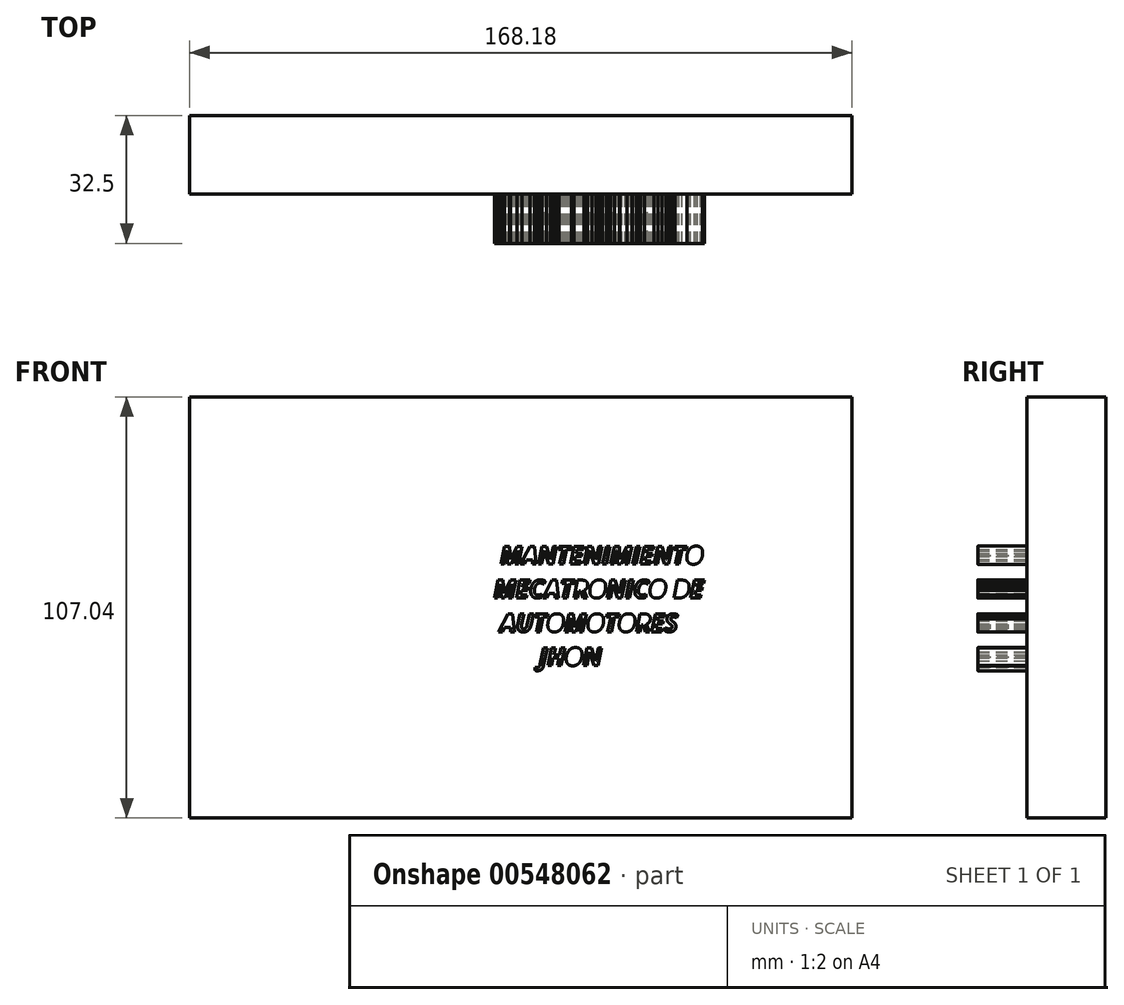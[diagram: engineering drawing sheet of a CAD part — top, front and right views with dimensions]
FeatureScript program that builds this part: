
annotation { "Feature Type Name" : "Feature", "Feature Type Description" : "" }
export const myFeature = defineFeature(function(context is Context, id is Id, definition is map)
    precondition{}
    {
        {
            var Q0;
            Q0=qCreatedBy(makeId("Front.planeOp"),FACE);
            var sketch = newSketch(context, id + "F0", { "sketchPlane" : qUnion([Q0])});
            skLineSegment(sketch, "E0.bottom", {"start": v(71.6, 53.52) * mm, "end": v(-71.6, 53.52) * mm});
            skLineSegment(sketch, "E0.top", {"start": v(71.6, -53.52) * mm, "end": v(-71.6, -53.52) * mm});
            skLineSegment(sketch, "E0.left", {"start": v(71.6, 53.52) * mm, "end": v(71.6, -53.52) * mm});
            skLineSegment(sketch, "E0.right", {"start": v(-71.6, 53.52) * mm, "end": v(-71.6, -53.52) * mm});
            skPoint(sketch, "E0.middle", {"position": v(0, 0) * mm});
            skSolve(sketch);
        }
        {
            var Q0;
            Q0=makeQuery(id+"F0.imprint","IMPRINT",FACE,{"disambiguationData":[TD([[makeQuery(id+"F0.imprint","IMPRINT",EDGE,{"derivedFrom":sQuery(id+"F0.wireOp",EDGE,"E0.bottom")}),1.0]])]});
            extrude(context, id + "F1", {"entities" : qUnion([Q0]), "depth" : 20 * mm, "offsetDistance" : 25 * mm});
        }
        {
            var Q0;
            Q0=makeQuery(id+"F1.opExtrude","CAP_FACE",FACE,{"disambiguationData":[OSD([sQuery(id+"F0.wireOp",EDGE,"E0.bottom"),sQuery(id+"F0.wireOp",EDGE,"E0.top"),sQuery(id+"F0.wireOp",EDGE,"E0.left"),sQuery(id+"F0.wireOp",EDGE,"E0.right")])],"isStart":false});
            var sketch = newSketch(context, id + "F2", { "sketchPlane" : qUnion([Q0])});
            skText(sketch, "E1", { "text": "         MANTENIMIENTO  \n        MECATRONICO DE \n         AUTOMOTORES \n               JHON ", "fontName": "OpenSans-BoldItalic.ttf"});
            const initialGuessF2  = {"E1": [-0.0325, 0.01102, 1, 0, 0.00455]};
            skSetInitialGuess(sketch, initialGuessF2);
            skSolve(sketch);
        }
        {
            var Q0;
            Q0=makeQuery(id+"F1.opExtrude","SWEPT_FACE",FACE,{"disambiguationData":[OSD([sQuery(id+"F0.wireOp",EDGE,"E0.right")])]});
            extrude(context, id + "F3", {"entities" : qUnion([Q0]), "operationType" : NewBodyOperationType.ADD, "depth" : 25 * mm, "offsetDistance" : 25 * mm});
        }
        {
            var Q0;
            Q0 = qSketchRegion(id + "F2", true);
            var Q1;
            Q1=makeQuery(id+"F2.imprint","IMPRINT",FACE,{"disambiguationData":[TD([[makeQuery(id+"F2.imprint","IMPRINT",EDGE,{"derivedFrom":sQuery(id+"F2.wireOp",EDGE,"E1.sketch_text.stroke-262")}),1.0]])]});
            var Q2;
            Q2=makeQuery(id+"F2.imprint","IMPRINT",FACE,{"disambiguationData":[TD([[makeQuery(id+"F2.imprint","IMPRINT",EDGE,{"derivedFrom":sQuery(id+"F2.wireOp",EDGE,"E1.sketch_text.stroke-181")}),-1.0]])]});
            var Q3;
            Q3=makeQuery(id+"F2.imprint","IMPRINT",FACE,{"disambiguationData":[TD([[makeQuery(id+"F2.imprint","IMPRINT",EDGE,{"derivedFrom":sQuery(id+"F2.wireOp",EDGE,"E1.sketch_text.stroke-32")}),-1.0]])]});
            var Q4;
            Q4=makeQuery(id+"F2.imprint","IMPRINT",FACE,{"disambiguationData":[TD([[makeQuery(id+"F2.imprint","IMPRINT",EDGE,{"derivedFrom":sQuery(id+"F2.wireOp",EDGE,"E1.sketch_text.stroke-511")}),-1.0]])]});
            var Q5;
            Q5=makeQuery(id+"F2.imprint","IMPRINT",FACE,{"disambiguationData":[TD([[makeQuery(id+"F2.imprint","IMPRINT",EDGE,{"derivedFrom":sQuery(id+"F2.wireOp",EDGE,"E1.sketch_text.stroke-67")}),-1.0]])]});
            var Q6;
            Q6=makeQuery(id+"F2.imprint","IMPRINT",FACE,{"disambiguationData":[TD([[makeQuery(id+"F2.imprint","IMPRINT",EDGE,{"derivedFrom":sQuery(id+"F2.wireOp",EDGE,"E1.sketch_text.stroke-104")}),-1.0]])]});
            var Q7;
            Q7=makeQuery(id+"F2.imprint","IMPRINT",FACE,{"disambiguationData":[TD([[makeQuery(id+"F2.imprint","IMPRINT",EDGE,{"derivedFrom":sQuery(id+"F2.wireOp",EDGE,"E1.sketch_text.stroke-153")}),1.0]])]});
            var Q8;
            Q8=makeQuery(id+"F2.imprint","IMPRINT",FACE,{"disambiguationData":[TD([[makeQuery(id+"F2.imprint","IMPRINT",EDGE,{"derivedFrom":sQuery(id+"F2.wireOp",EDGE,"E1.sketch_text.stroke-470")}),1.0]])]});
            var Q9;
            Q9=makeQuery(id+"F2.imprint","IMPRINT",FACE,{"disambiguationData":[TD([[makeQuery(id+"F2.imprint","IMPRINT",EDGE,{"derivedFrom":sQuery(id+"F2.wireOp",EDGE,"E1.sketch_text.stroke-452")}),-1.0]])]});
            var Q10;
            Q10=makeQuery(id+"F2.imprint","IMPRINT",FACE,{"disambiguationData":[TD([[makeQuery(id+"F2.imprint","IMPRINT",EDGE,{"derivedFrom":sQuery(id+"F2.wireOp",EDGE,"E1.sketch_text.stroke-442")}),1.0]])]});
            var Q11;
            Q11=makeQuery(id+"F2.imprint","IMPRINT",FACE,{"disambiguationData":[TD([[makeQuery(id+"F2.imprint","IMPRINT",EDGE,{"derivedFrom":sQuery(id+"F2.wireOp",EDGE,"E1.sketch_text.stroke-337")}),1.0]])]});
            var Q12;
            Q12=makeQuery(id+"F2.imprint","IMPRINT",FACE,{"disambiguationData":[TD([[makeQuery(id+"F2.imprint","IMPRINT",EDGE,{"derivedFrom":sQuery(id+"F2.wireOp",EDGE,"E1.sketch_text.stroke-319")}),1.0]])]});
            var Q13;
            Q13=makeQuery(id+"F2.imprint","IMPRINT",FACE,{"disambiguationData":[TD([[makeQuery(id+"F2.imprint","IMPRINT",EDGE,{"derivedFrom":sQuery(id+"F2.wireOp",EDGE,"E1.sketch_text.stroke-567")}),1.0]])]});
            var Q14;
            Q14=makeQuery(id+"F2.imprint","IMPRINT",FACE,{"disambiguationData":[TD([[makeQuery(id+"F2.imprint","IMPRINT",EDGE,{"derivedFrom":sQuery(id+"F2.wireOp",EDGE,"E1.sketch_text.stroke-432")}),-1.0]])]});
            var Q15;
            Q15=makeQuery(id+"F2.imprint","IMPRINT",FACE,{"disambiguationData":[TD([[makeQuery(id+"F2.imprint","IMPRINT",EDGE,{"derivedFrom":sQuery(id+"F2.wireOp",EDGE,"E1.sketch_text.stroke-480")}),1.0]])]});
            var Q16;
            Q16=makeQuery(id+"F2.imprint","IMPRINT",FACE,{"disambiguationData":[TD([[makeQuery(id+"F2.imprint","IMPRINT",EDGE,{"derivedFrom":sQuery(id+"F2.wireOp",EDGE,"E1.sketch_text.stroke-460")}),-1.0]])]});
            var Q17;
            Q17=makeQuery(id+"F2.imprint","IMPRINT",FACE,{"disambiguationData":[TD([[makeQuery(id+"F2.imprint","IMPRINT",EDGE,{"derivedFrom":sQuery(id+"F2.wireOp",EDGE,"E1.sketch_text.stroke-499")}),-1.0]])]});
            var Q18;
            Q18=makeQuery(id+"F2.imprint","IMPRINT",FACE,{"disambiguationData":[TD([[makeQuery(id+"F2.imprint","IMPRINT",EDGE,{"derivedFrom":sQuery(id+"F2.wireOp",EDGE,"E1.sketch_text.stroke-193")}),-1.0]])]});
            var Q19;
            Q19=makeQuery(id+"F2.imprint","IMPRINT",FACE,{"disambiguationData":[TD([[makeQuery(id+"F2.imprint","IMPRINT",EDGE,{"derivedFrom":sQuery(id+"F2.wireOp",EDGE,"E1.sketch_text.stroke-163")}),-1.0]])]});
            var Q20;
            Q20=makeQuery(id+"F2.imprint","IMPRINT",FACE,{"disambiguationData":[TD([[makeQuery(id+"F2.imprint","IMPRINT",EDGE,{"derivedFrom":sQuery(id+"F2.wireOp",EDGE,"E1.sketch_text.stroke-0")}),-1.0]])]});
            var Q21;
            Q21=makeQuery(id+"F2.imprint","IMPRINT",FACE,{"disambiguationData":[TD([[makeQuery(id+"F2.imprint","IMPRINT",EDGE,{"derivedFrom":sQuery(id+"F2.wireOp",EDGE,"E1.sketch_text.stroke-47")}),-1.0]])]});
            var Q22;
            Q22=makeQuery(id+"F2.imprint","IMPRINT",FACE,{"disambiguationData":[TD([[makeQuery(id+"F2.imprint","IMPRINT",EDGE,{"derivedFrom":sQuery(id+"F2.wireOp",EDGE,"E1.sketch_text.stroke-55")}),-1.0]])]});
            var Q23;
            Q23=makeQuery(id+"F2.imprint","IMPRINT",FACE,{"disambiguationData":[TD([[makeQuery(id+"F2.imprint","IMPRINT",EDGE,{"derivedFrom":sQuery(id+"F2.wireOp",EDGE,"E1.sketch_text.stroke-480")}),-1.0]])]});
            var Q24;
            Q24=makeQuery(id+"F2.imprint","IMPRINT",FACE,{"disambiguationData":[TD([[makeQuery(id+"F2.imprint","IMPRINT",EDGE,{"derivedFrom":sQuery(id+"F2.wireOp",EDGE,"E1.sketch_text.stroke-272")}),-1.0]])]});
            var Q25;
            Q25=makeQuery(id+"F2.imprint","IMPRINT",FACE,{"disambiguationData":[TD([[makeQuery(id+"F2.imprint","IMPRINT",EDGE,{"derivedFrom":sQuery(id+"F2.wireOp",EDGE,"E1.sketch_text.stroke-82")}),-1.0]])]});
            var Q26;
            Q26=makeQuery(id+"F2.imprint","IMPRINT",FACE,{"disambiguationData":[TD([[makeQuery(id+"F2.imprint","IMPRINT",EDGE,{"derivedFrom":sQuery(id+"F2.wireOp",EDGE,"E1.sketch_text.stroke-86")}),-1.0]])]});
            var Q27;
            Q27=makeQuery(id+"F2.imprint","IMPRINT",FACE,{"disambiguationData":[TD([[makeQuery(id+"F2.imprint","IMPRINT",EDGE,{"derivedFrom":sQuery(id+"F2.wireOp",EDGE,"E1.sketch_text.stroke-108")}),-1.0]])]});
            var Q28;
            Q28=makeQuery(id+"F2.imprint","IMPRINT",FACE,{"disambiguationData":[TD([[makeQuery(id+"F2.imprint","IMPRINT",EDGE,{"derivedFrom":sQuery(id+"F2.wireOp",EDGE,"E1.sketch_text.stroke-120")}),-1.0]])]});
            var Q29;
            Q29=makeQuery(id+"F2.imprint","IMPRINT",FACE,{"disambiguationData":[TD([[makeQuery(id+"F2.imprint","IMPRINT",EDGE,{"derivedFrom":sQuery(id+"F2.wireOp",EDGE,"E1.sketch_text.stroke-135")}),-1.0]])]});
            var Q30;
            Q30=makeQuery(id+"F2.imprint","IMPRINT",FACE,{"disambiguationData":[TD([[makeQuery(id+"F2.imprint","IMPRINT",EDGE,{"derivedFrom":sQuery(id+"F2.wireOp",EDGE,"E1.sketch_text.stroke-557")}),-1.0]])]});
            var Q31;
            Q31=makeQuery(id+"F2.imprint","IMPRINT",FACE,{"disambiguationData":[TD([[makeQuery(id+"F2.imprint","IMPRINT",EDGE,{"derivedFrom":sQuery(id+"F2.wireOp",EDGE,"E1.sketch_text.stroke-535")}),-1.0]])]});
            var Q32;
            Q32=makeQuery(id+"F2.imprint","IMPRINT",FACE,{"disambiguationData":[TD([[makeQuery(id+"F2.imprint","IMPRINT",EDGE,{"derivedFrom":sQuery(id+"F2.wireOp",EDGE,"E1.sketch_text.stroke-287")}),-1.0]])]});
            var Q33;
            Q33=makeQuery(id+"F2.imprint","IMPRINT",FACE,{"disambiguationData":[TD([[makeQuery(id+"F2.imprint","IMPRINT",EDGE,{"derivedFrom":sQuery(id+"F2.wireOp",EDGE,"E1.sketch_text.stroke-225")}),-1.0]])]});
            var Q34;
            Q34=makeQuery(id+"F2.imprint","IMPRINT",FACE,{"disambiguationData":[TD([[makeQuery(id+"F2.imprint","IMPRINT",EDGE,{"derivedFrom":sQuery(id+"F2.wireOp",EDGE,"E1.sketch_text.stroke-394")}),-1.0]])]});
            var Q35;
            Q35=makeQuery(id+"F2.imprint","IMPRINT",FACE,{"disambiguationData":[TD([[makeQuery(id+"F2.imprint","IMPRINT",EDGE,{"derivedFrom":sQuery(id+"F2.wireOp",EDGE,"E1.sketch_text.stroke-357")}),-1.0]])]});
            var Q36;
            Q36=makeQuery(id+"F2.imprint","IMPRINT",FACE,{"disambiguationData":[TD([[makeQuery(id+"F2.imprint","IMPRINT",EDGE,{"derivedFrom":sQuery(id+"F2.wireOp",EDGE,"E1.sketch_text.stroke-414")}),-1.0]])]});
            var Q37;
            Q37=makeQuery(id+"F2.imprint","IMPRINT",FACE,{"disambiguationData":[TD([[makeQuery(id+"F2.imprint","IMPRINT",EDGE,{"derivedFrom":sQuery(id+"F2.wireOp",EDGE,"E1.sketch_text.stroke-309")}),-1.0]])]});
            var Q38;
            Q38=makeQuery(id+"F2.imprint","IMPRINT",FACE,{"disambiguationData":[TD([[makeQuery(id+"F2.imprint","IMPRINT",EDGE,{"derivedFrom":sQuery(id+"F2.wireOp",EDGE,"E1.sketch_text.stroke-404")}),1.0]])]});
            var Q39;
            Q39=makeQuery(id+"F2.imprint","IMPRINT",FACE,{"disambiguationData":[TD([[makeQuery(id+"F2.imprint","IMPRINT",EDGE,{"derivedFrom":sQuery(id+"F2.wireOp",EDGE,"E1.sketch_text.stroke-252")}),-1.0]])]});
            var Q40;
            Q40=makeQuery(id+"F2.imprint","IMPRINT",FACE,{"disambiguationData":[TD([[makeQuery(id+"F2.imprint","IMPRINT",EDGE,{"derivedFrom":sQuery(id+"F2.wireOp",EDGE,"E1.sketch_text.stroke-329")}),-1.0]])]});
            var Q41;
            Q41=makeQuery(id+"F2.imprint","IMPRINT",FACE,{"disambiguationData":[TD([[makeQuery(id+"F2.imprint","IMPRINT",EDGE,{"derivedFrom":sQuery(id+"F2.wireOp",EDGE,"E1.sketch_text.stroke-386")}),-1.0]])]});
            var Q42;
            Q42=makeQuery(id+"F2.imprint","IMPRINT",FACE,{"disambiguationData":[TD([[makeQuery(id+"F2.imprint","IMPRINT",EDGE,{"derivedFrom":sQuery(id+"F2.wireOp",EDGE,"E1.sketch_text.stroke-233")}),-1.0]])]});
            var Q43;
            Q43=makeQuery(id+"F2.imprint","IMPRINT",FACE,{"disambiguationData":[TD([[makeQuery(id+"F2.imprint","IMPRINT",EDGE,{"derivedFrom":sQuery(id+"F2.wireOp",EDGE,"E1.sketch_text.stroke-371")}),-1.0]])]});
            var Q44;
            Q44=makeQuery(id+"F2.imprint","IMPRINT",FACE,{"disambiguationData":[TD([[makeQuery(id+"F2.imprint","IMPRINT",EDGE,{"derivedFrom":sQuery(id+"F2.wireOp",EDGE,"E1.sketch_text.stroke-211")}),-1.0]])]});
            var Q45;
            Q45=makeQuery(id+"F2.imprint","IMPRINT",FACE,{"disambiguationData":[TD([[makeQuery(id+"F2.imprint","IMPRINT",EDGE,{"derivedFrom":sQuery(id+"F2.wireOp",EDGE,"E1.sketch_text.stroke-365")}),1.0]])]});
            var Q46;
            Q46=makeQuery(id+"F2.imprint","IMPRINT",FACE,{"disambiguationData":[TD([[makeQuery(id+"F2.imprint","IMPRINT",EDGE,{"derivedFrom":sQuery(id+"F2.wireOp",EDGE,"E1.sketch_text.stroke-143")}),-1.0]])]});
            var Q47;
            Q47=makeQuery(id+"F2.imprint","IMPRINT",FACE,{"disambiguationData":[TD([[makeQuery(id+"F2.imprint","IMPRINT",EDGE,{"derivedFrom":sQuery(id+"F2.wireOp",EDGE,"E1.sketch_text.stroke-345")}),-1.0]])]});
            var Q48;
            Q48=makeQuery(id+"F2.imprint","IMPRINT",FACE,{"disambiguationData":[TD([[makeQuery(id+"F2.imprint","IMPRINT",EDGE,{"derivedFrom":sQuery(id+"F2.wireOp",EDGE,"E1.sketch_text.stroke-18")}),-1.0]])]});
            var Q49;
            Q49=makeQuery(id+"F2.imprint","IMPRINT",FACE,{"disambiguationData":[TD([[makeQuery(id+"F2.imprint","IMPRINT",EDGE,{"derivedFrom":sQuery(id+"F2.wireOp",EDGE,"E1.sketch_text.stroke-577")}),-1.0]])]});
            var Q50;
            Q50=makeQuery(id+"F2.imprint","IMPRINT",FACE,{"disambiguationData":[TD([[makeQuery(id+"F2.imprint","IMPRINT",EDGE,{"derivedFrom":sQuery(id+"F2.wireOp",EDGE,"E1.sketch_text.stroke-291")}),-1.0]])]});
            var Q51;
            Q51=makeQuery(id+"F2.imprint","IMPRINT",FACE,{"disambiguationData":[TD([[makeQuery(id+"F2.imprint","IMPRINT",EDGE,{"derivedFrom":sQuery(id+"F2.wireOp",EDGE,"E1.sketch_text.stroke-545")}),-1.0]])]});
            var Q52;
            Q52=makeQuery(id+"F2.imprint","IMPRINT",FACE,{"disambiguationData":[TD([[makeQuery(id+"F2.imprint","IMPRINT",EDGE,{"derivedFrom":sQuery(id+"F2.wireOp",EDGE,"E1.sketch_text.stroke-233")}),1.0]])]});
            var Q53;
            Q53=makeQuery(id+"F2.imprint","IMPRINT",FACE,{"disambiguationData":[TD([[makeQuery(id+"F2.imprint","IMPRINT",EDGE,{"derivedFrom":sQuery(id+"F2.wireOp",EDGE,"E1.sketch_text.stroke-26")}),1.0]])]});
            var Q54;
            Q54=makeQuery(id+"F2.imprint","IMPRINT",FACE,{"disambiguationData":[TD([[makeQuery(id+"F2.imprint","IMPRINT",EDGE,{"derivedFrom":sQuery(id+"F2.wireOp",EDGE,"E1.sketch_text.stroke-219")}),1.0]])]});
            extrude(context, id + "F4", {"entities" : qUnion([Q0, Q1, Q2, Q3, Q4, Q5, Q6, Q7, Q8, Q9, Q10, Q11, Q12, Q13, Q14, Q15, Q16, Q17, Q18, Q19, Q20, Q21, Q22, Q23, Q24, Q25, Q26, Q27, Q28, Q29, Q30, Q31, Q32, Q33, Q34, Q35, Q36, Q37, Q38, Q39, Q40, Q41, Q42, Q43, Q44, Q45, Q46, Q47, Q48, Q49, Q50, Q51, Q52, Q53, Q54]), "operationType" : NewBodyOperationType.ADD, "endBound" : BoundingType.SYMMETRIC, "depth" : 25 * mm, "offsetDistance" : 25 * mm});
        }
    });
